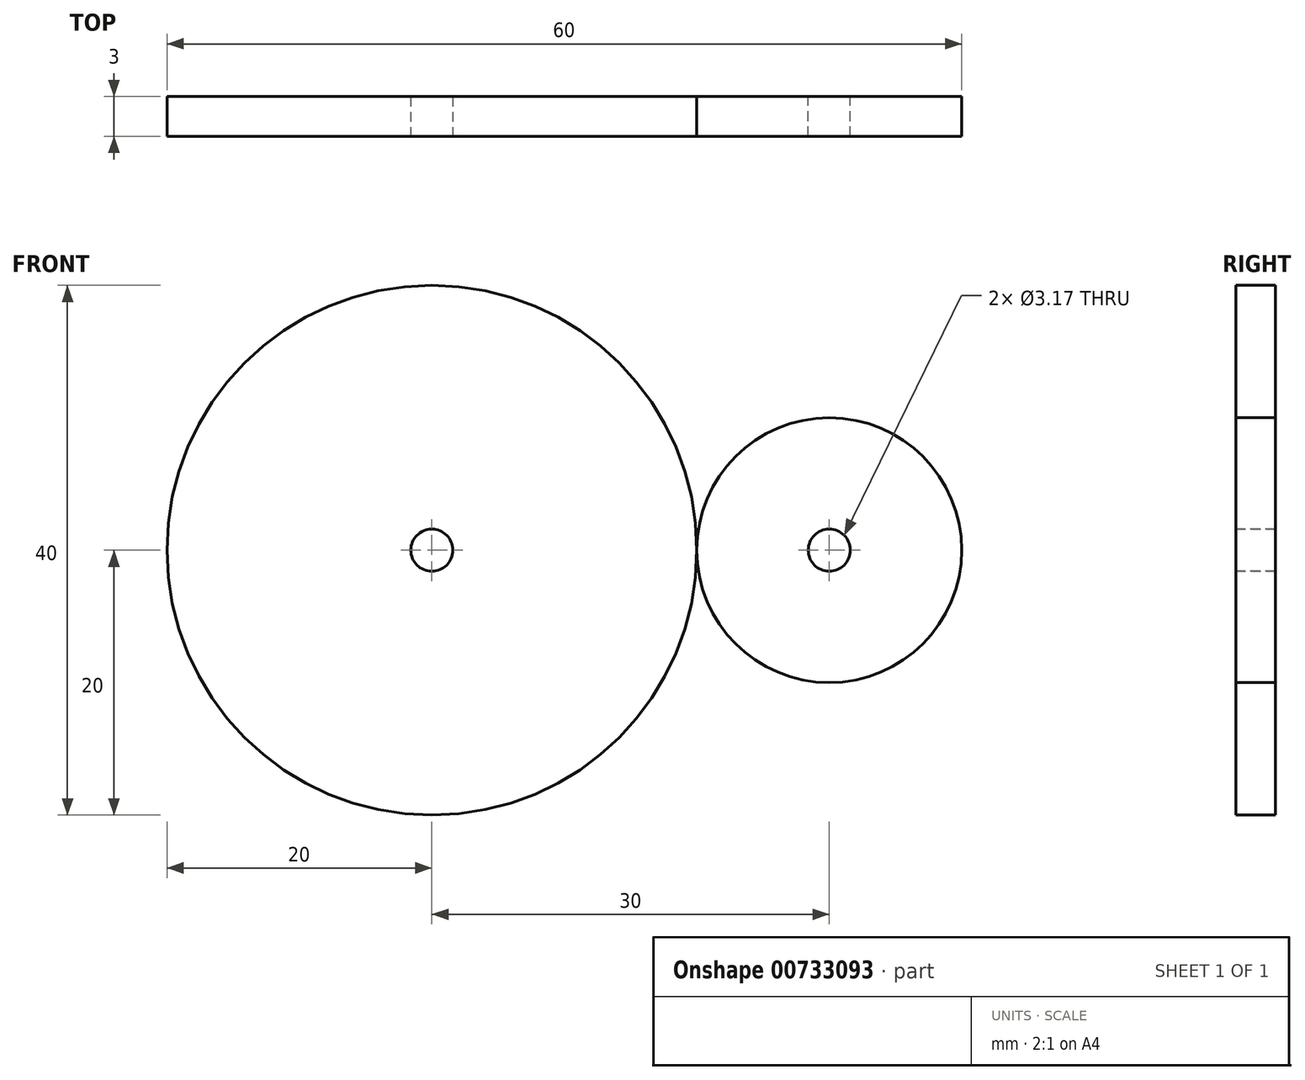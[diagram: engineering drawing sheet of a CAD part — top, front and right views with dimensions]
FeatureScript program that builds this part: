
annotation { "Feature Type Name" : "Feature", "Feature Type Description" : "" }
export const myFeature = defineFeature(function(context is Context, id is Id, definition is map)
    precondition{}
    {
        {
            var Q0;
            Q0=qCreatedBy(makeId("Front.planeOp"),FACE);
            var sketch = newSketch(context, id + "F0", { "sketchPlane" : qUnion([Q0])});
            skCircle(sketch, "E0", {"center": v(0, 0) * mm, "radius": 20 * mm});
            skLineSegment(sketch, "E1", {"start": v(20, 0) * mm, "end": v(40, 0) * mm});
            skPoint(sketch, "E2", {"position": v(30, 0) * mm});
            skCircle(sketch, "E3", {"center": v(30, 0) * mm, "radius": 10 * mm});
            skSolve(sketch);
        }
        {
            var Q0;
            Q0=makeQuery(id+"F0.imprint","IMPRINT",FACE,{"disambiguationData":[TD([[makeQuery(id+"F0.imprint","IMPRINT",EDGE,{"derivedFrom":sQuery(id+"F0.wireOp",EDGE,"E0")}),1.0]])]});
            var Q1;
            {var subQ0=sQuery(id+"F0.wireOp",EDGE,"E1");Q1=makeQuery(id+"F0.imprint","IMPRINT",FACE,{"disambiguationData":[TD([[makeQuery(id+"F0.imprint","IMPRINT",EDGE,{"derivedFrom":subQ0}),1.0]])]});}
            var Q2;
            {var subQ0=sQuery(id+"F0.wireOp",EDGE,"E1");Q2=makeQuery(id+"F0.imprint","IMPRINT",FACE,{"disambiguationData":[TD([[makeQuery(id+"F0.imprint","IMPRINT",EDGE,{"derivedFrom":subQ0}),-1.0]])]});}
            extrude(context, id + "F1", {"entities" : qUnion([Q0, Q1, Q2]), "depth" : 3 * mm, "offsetDistance" : 25.4 * mm});
        }
        {
            var Q0;
            Q0=makeQuery(id+"F1.opExtrude","CAP_FACE",FACE,{"disambiguationData":[OSD([sQuery(id+"F0.wireOp",EDGE,"E0")])],"isStart":false});
            var sketch = newSketch(context, id + "F2", { "sketchPlane" : qUnion([Q0])});
            skCircle(sketch, "E4", {"center": v(0, 0) * mm, "radius": 1.59 * mm});
            skSolve(sketch);
        }
        {
            var Q0;
            Q0=makeQuery(id+"F2.imprint","IMPRINT",FACE,{"disambiguationData":[TD([[makeQuery(id+"F2.imprint","IMPRINT",EDGE,{"derivedFrom":sQuery(id+"F2.wireOp",EDGE,"E4")}),1.0]])]});
            extrude(context, id + "F3", {"entities" : qUnion([Q0]), "operationType" : NewBodyOperationType.REMOVE, "oppositeDirection" : true, "depth" : 25.4 * mm, "offsetDistance" : 25.4 * mm});
        }
        {
            var Q0;
            Q0=makeQuery(id+"F1.opExtrude","CAP_FACE",FACE,{"disambiguationData":[OSD([sQuery(id+"F0.wireOp",EDGE,"E3")])],"isStart":true});
            var sketch = newSketch(context, id + "F4", { "sketchPlane" : qUnion([Q0])});
            skCircle(sketch, "E5", {"center": v(-30, 0) * mm, "radius": 1.59 * mm});
            skSolve(sketch);
        }
        {
            var Q0;
            Q0=makeQuery(id+"F4.imprint","IMPRINT",FACE,{"disambiguationData":[TD([[makeQuery(id+"F4.imprint","IMPRINT",EDGE,{"derivedFrom":sQuery(id+"F4.wireOp",EDGE,"E5")}),1.0]])]});
            extrude(context, id + "F5", {"entities" : qUnion([Q0]), "operationType" : NewBodyOperationType.REMOVE, "oppositeDirection" : true, "depth" : 25.4 * mm, "offsetDistance" : 25.4 * mm});
        }
    });
